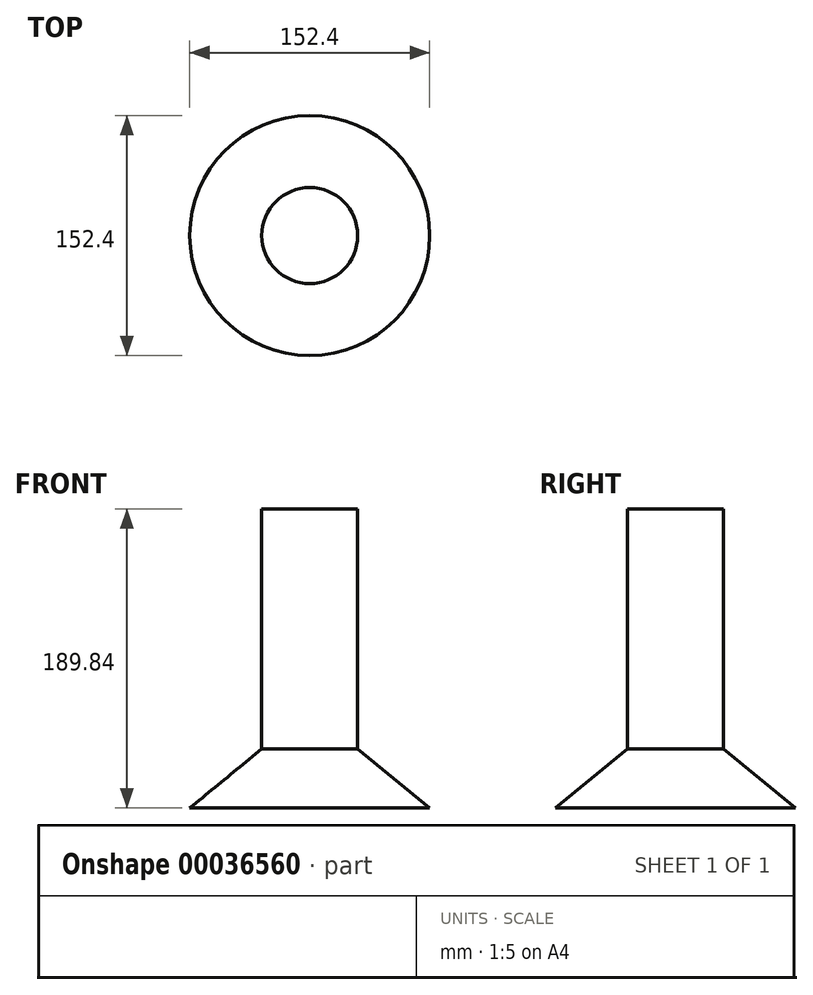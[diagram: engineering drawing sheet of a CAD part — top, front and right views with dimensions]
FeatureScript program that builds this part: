
annotation { "Feature Type Name" : "Feature", "Feature Type Description" : "" }
export const myFeature = defineFeature(function(context is Context, id is Id, definition is map)
    precondition{}
    {
        {
            var Q0;
            Q0=qCreatedBy(makeId("Front.planeOp"),FACE);
            var sketch = newSketch(context, id + "F0", { "sketchPlane" : qUnion([Q0])});
            skLineSegment(sketch, "E0", {"start": v(0, -164.1) * mm, "end": v(0, 140.05) * mm, "construction": true});
            skLineSegment(sketch, "E1.bottom", {"start": v(0, 99) * mm, "end": v(30.48, 99) * mm});
            skLineSegment(sketch, "E1.top", {"start": v(0, -53.4) * mm, "end": v(30.48, -53.4) * mm});
            skLineSegment(sketch, "E1.left", {"start": v(0, 99) * mm, "end": v(0, -53.4) * mm});
            skLineSegment(sketch, "E1.right", {"start": v(30.48, 99) * mm, "end": v(30.48, -53.4) * mm});
            skLineSegment(sketch, "E2", {"start": v(30.48, -53.4) * mm, "end": v(76.2, -90.85) * mm});
            skLineSegment(sketch, "E3", {"start": v(76.2, -90.85) * mm, "end": v(0, -90.85) * mm});
            skLineSegment(sketch, "E4", {"start": v(0, -90.85) * mm, "end": v(0, -53.4) * mm});
            skSolve(sketch);
        }
        {
            var Q0;
            Q0=makeQuery(id+"F0.imprint","IMPRINT",FACE,{"disambiguationData":[TD([[makeQuery(id+"F0.imprint","IMPRINT",EDGE,{"derivedFrom":sQuery(id+"F0.wireOp",EDGE,"E1.top")}),-1.0]])]});
            var Q1;
            Q1=makeQuery(id+"F0.imprint","IMPRINT",FACE,{"disambiguationData":[TD([[makeQuery(id+"F0.imprint","IMPRINT",EDGE,{"derivedFrom":sQuery(id+"F0.wireOp",EDGE,"E1.bottom")}),-1.0]])]});
            var Q2;
            Q2=sQuery(id+"F0.wireOp",EDGE,"E0");
            revolve(context, id + "F1", {"entities" : qUnion([Q0, Q1]), "axis" : qUnion([Q2]), "revolveType" : RevolveType.FULL});
        }
    });
